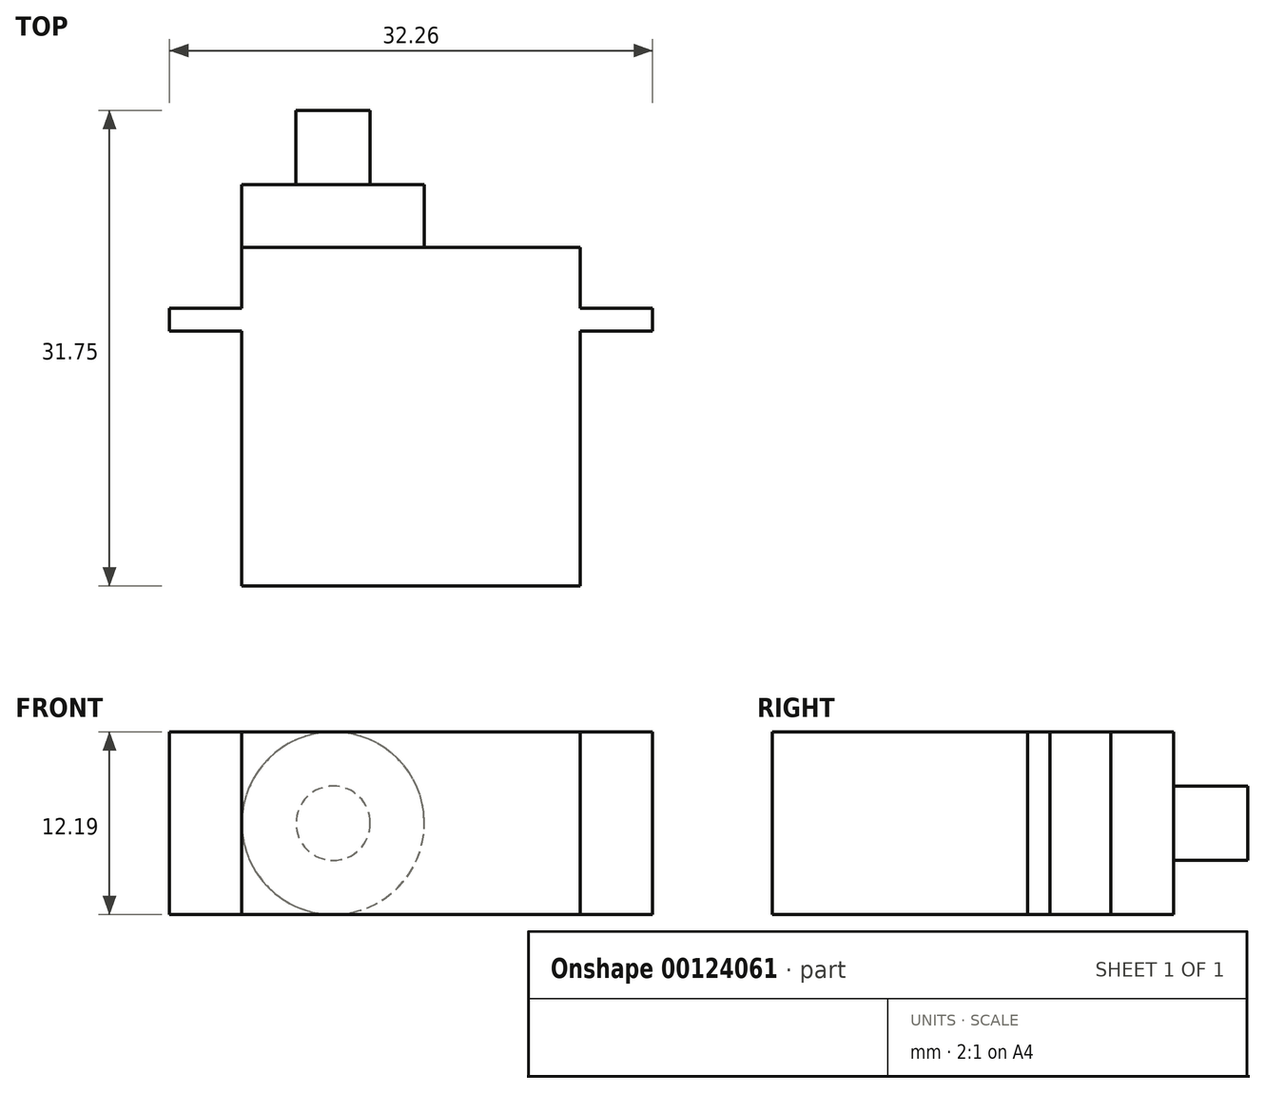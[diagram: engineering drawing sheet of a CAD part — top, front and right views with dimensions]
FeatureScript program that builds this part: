
annotation { "Feature Type Name" : "Feature", "Feature Type Description" : "" }
export const myFeature = defineFeature(function(context is Context, id is Id, definition is map)
    precondition{}
    {
        {
            var Q0;
            Q0=qCreatedBy(makeId("Top.planeOp"),FACE);
            var sketch = newSketch(context, id + "F0", { "sketchPlane" : qUnion([Q0])});
            skLineSegment(sketch, "E0", {"start": v(0, 0) * mm, "end": v(0, 17.03) * mm});
            skLineSegment(sketch, "E1", {"start": v(0, 17.03) * mm, "end": v(-4.83, 17.03) * mm});
            skLineSegment(sketch, "E2", {"start": v(-4.83, 17.03) * mm, "end": v(-4.83, 18.54) * mm});
            skLineSegment(sketch, "E3", {"start": v(-4.83, 18.54) * mm, "end": v(0, 18.54) * mm});
            skLineSegment(sketch, "E4", {"start": v(0, 18.54) * mm, "end": v(0, 22.6) * mm});
            skLineSegment(sketch, "E5", {"start": v(0, 22.6) * mm, "end": v(22.6, 22.6) * mm});
            skLineSegment(sketch, "E6", {"start": v(22.6, 22.6) * mm, "end": v(22.6, 18.54) * mm});
            skLineSegment(sketch, "E7", {"start": v(22.6, 18.54) * mm, "end": v(27.43, 18.54) * mm});
            skLineSegment(sketch, "E8", {"start": v(27.43, 18.54) * mm, "end": v(27.43, 17.03) * mm});
            skLineSegment(sketch, "E9", {"start": v(27.43, 17.03) * mm, "end": v(22.6, 17.03) * mm});
            skLineSegment(sketch, "E10", {"start": v(22.6, 17.03) * mm, "end": v(22.6, 0) * mm});
            skLineSegment(sketch, "E11", {"start": v(22.6, 0) * mm, "end": v(0, 0) * mm});
            skSolve(sketch);
        }
        {
            var Q0;
            Q0 = qSketchRegion(id + "F0", true);
            extrude(context, id + "F1", {"entities" : qUnion([Q0]), "depth" : 12.2 * mm});
        }
        {
            var Q0;
            Q0=makeQuery(id+"F1.opExtrude","SWEPT_FACE",FACE,{"disambiguationData":[OSD([sQuery(id+"F0.wireOp",EDGE,"E5")])]});
            var sketch = newSketch(context, id + "F2", { "sketchPlane" : qUnion([Q0])});
            skPoint(sketch, "E12", {"position": v(-6.1, 6.1) * mm});
            skCircle(sketch, "E13", {"center": v(-6.1, 6.1) * mm, "radius": 6.1 * mm});
            skSolve(sketch);
        }
        {
            var Q0;
            Q0 = qSketchRegion(id + "F2", true);
            extrude(context, id + "F3", {"entities" : qUnion([Q0]), "operationType" : NewBodyOperationType.ADD, "depth" : 4.2 * mm});
        }
        {
            var Q0;
            Q0=makeQuery(id+"F3.opExtrude","CAP_FACE",FACE,{"disambiguationData":[OSD([sQuery(id+"F2.wireOp",EDGE,"E13")])],"isStart":false});
            var sketch = newSketch(context, id + "F4", { "sketchPlane" : qUnion([Q0])});
            skPoint(sketch, "E14", {"position": v(-6.1, 6.1) * mm});
            skCircle(sketch, "E15", {"center": v(-6.1, 6.1) * mm, "radius": 2.48 * mm});
            skSolve(sketch);
        }
        {
            var Q0;
            Q0 = qSketchRegion(id + "F4", true);
            extrude(context, id + "F5", {"entities" : qUnion([Q0]), "operationType" : NewBodyOperationType.ADD, "depth" : 4.95 * mm});
        }
    });
